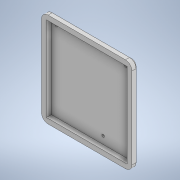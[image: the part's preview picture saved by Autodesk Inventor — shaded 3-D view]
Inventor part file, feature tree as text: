
AUTODESK INVENTOR PART (.ipt)
format: ipt  version: 2021 (Build 250183000, 183)  size: 133,120 bytes
history: native  units: mm
features: extrude x2, sketch x1, fillet x1, chamfer x1
ambient origin geometry x8: Origin, YZ Plane, XZ Plane, XY Plane, X Axis, Y Axis, Z Axis, Center Point
bodies: Solid1 (feature_tree)
feature tree (5):
  sketch  "Sketch1"  dims[d0=2.0mm d1=4.0mm d2=8.0mm d3=0.0mm d4=2.0mm d5=0.0mm d6=8.0mm d7=3.0mm d8=2.0mm d9=45.0deg]
  extrude  "Extrusion1"  Depth=8.0mm TaperAngle=0.0deg
  extrude  "Extrusion2"  Depth=2.0mm TaperAngle=0.0deg
  fillet  "Fillet1"  Radius=8.0mm
  chamfer  "Chamfer1"  Distance=2.0mm Angle=45.0deg
